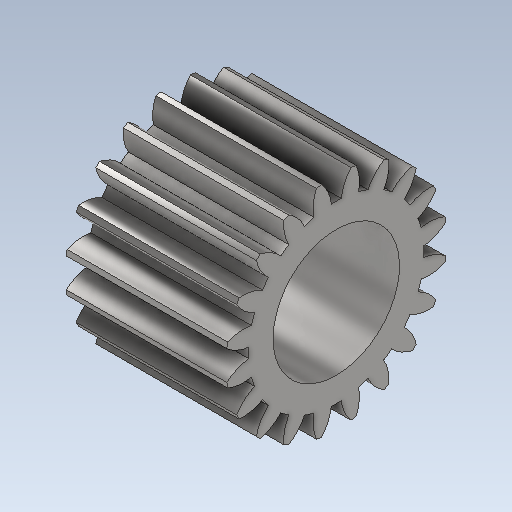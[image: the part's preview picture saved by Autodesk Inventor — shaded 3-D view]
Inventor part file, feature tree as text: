
AUTODESK INVENTOR PART (.ipt)
format: ipt  version: 2023 (Build 270158000, 158)  size: 600,576 bytes
history: native  units: in
note: dims shown in document units (in); Inventor stores cm internally (conversion verified against a paired STEP export)
features: extrude x2, sketch x2, other x1
ambient origin geometry x8: Origin, YZ Plane, XZ Plane, XY Plane, X Axis, Y Axis, Z Axis, Center Point
bodies: Solid1 (feature_tree)
feature tree (5):
  extrude  "Extrusion1"  TaperAngle=0.0deg  [1 undecoded]
  extrude  "Extrusion2"  TaperAngle=0.0deg  [1 undecoded]
  sketch  "Sketch1"  dims[d0=0.5in d1=0.0in d2=0.0in]
  sketch  "Sketch2"  dims[d4=0.3937in d5=0.0in d6=0.0in]
  other  "TeethCuts"
note: 2 required parameter values undecoded (feature->parameter linkage not recoverable at this tier; creation-order binding heuristic only, values carry confidence <= 0.55)
